# Revit family: Levelers_Serco_RM-VSL
name_source: partatom
category: Generic Models
units: mm (PartAtom-declared; Revit-internal decimal feet)

## family parameters
Always vertical = Yes
Can host rebar = No
Cut with Voids When Loaded = Yes
Host = Floor
Maintain Annotation Orientation = No
Part Type = Normal
Room Calculation Point = No
Round Connector Dimension = Use Diameter
Shared = No

## types (9) — shared parameters
BumperPlateHeight = 2' - 4"
BumperPlateWidth = 1' - 0"
BumperProjection = 0' - 4"
BumperPudHeight = 1' - 8"
BumperPudWidth = 0' - 8"
Capacity = 40-50k
Default Elevation = 0' - 0"
Description = Vertically Stored Leveler
LipLength = 1' - 8"
Manufacturer = Entrematic
Model = VSL
Type Comments = Remote Motor, Pit Mount
URL = https://www.entrematic.us

## per-type parameters (varying)
| type | BollardHeight | BumperBelowDock | BumperDistance | EmbedWidth | Exclusion | LevelerLength | LevelerWidth | LipTaper | PitDepth | PitLength | PitWidth |
| 6x8 | 3' - 10" | 0' - 0" | 6' - 2" | 6' - 11 1/2" | 7' - 4" | 6' - 9 9/16" | 6' - 0" | 5' - 6" | 1' - 3" | 6' - 10 11/16" | 6' - 5 1/2" |
| 6x6 | 4' - 0" | 0' - 0" | 6' - 2" | 6' - 11 1/2" | 7' - 4" | 5' - 4" | 6' - 0" | 5' - 6" | 1' - 0" | 5' - 5 1/8" | 6' - 5 1/2" |
| 6x5 | 4' - 0" | 0' - 6" | 6' - 2" | 6' - 11 1/2" | 7' - 4" | 4' - 4" | 6' - 0" | 5' - 6" | 0' - 10" | 4' - 5 1/8" | 6' - 5 1/2" |
| 6.5x5 | 3' - 10" | 0' - 0" | 6' - 8" | 7' - 5 1/2" | 7' - 10" | 4' - 4" | 6' - 6" | 6' - 0" | 0' - 10" | 4' - 5 1/8" | 6' - 11 1/2" |
| 6.5x6 | 3' - 10" | 0' - 0" | 6' - 8" | 7' - 5 1/2" | 7' - 10" | 5' - 4" | 6' - 6" | 6' - 0" | 1' - 0" | 5' - 5 1/8" | 6' - 11 1/2" |
| 6.5x8 | 3' - 10" | 0' - 0" | 6' - 8" | 7' - 5 1/2" | 7' - 10" | 6' - 9 9/16" | 6' - 6" | 6' - 0" | 1' - 3" | 6' - 10 11/16" | 6' - 11 1/2" |
| 7x5 | 3' - 10" | 0' - 0" | 7' - 2" | 7' - 11 1/2" | 8' - 4" | 4' - 4" | 7' - 0" | 6' - 6" | 0' - 10" | 4' - 5 1/8" | 7' - 5 1/2" |
| 7x6 | 3' - 10" | 0' - 0" | 7' - 2" | 7' - 11 1/2" | 8' - 4" | 5' - 4" | 7' - 0" | 6' - 6" | 1' - 0" | 5' - 5 1/8" | 7' - 5 1/2" |
| 7x8 | 3' - 10" | 0' - 0" | 7' - 2" | 7' - 11 1/2" | 8' - 4" | 6' - 9 9/16" | 7' - 0" | 6' - 6" | 1' - 3" | 6' - 10 11/16" | 7' - 5 1/2" |

## geometry (parser evidence)
native form markers: Blend x4, Sweep x2
no freeform markers — native parametric forms only
